# Revit family: P300298-009
name_source: partatom
category: Lighting Fixtures
revit_build: Autodesk Revit 2017 (Build: 20160225_1515(x64)
units: mm (PartAtom-declared; Revit-internal decimal feet)

## family parameters
Cut with Voids When Loaded = No
Host = Face
Light Source = No
OmniClass Number = 23.80.70.11.14.17
OmniClass Title = Direct/Indirect
Part Type = Normal
Room Calculation Point = No
Round Connector Dimension = Use Diameter
Shared = Yes

## types (1)
- P300298-009
    Apparent Load = 100 VA
    Assembly Code = D5020200
    Connector Description = Lighting Connector
    Default Elevation = 48 "
    Description = Conway Collection Four-Light Brushed Nickel and Clear Seeded Farmhouse Style Bath Vanity Wall Light
    Features = Mix old and new for charming character with the Conway Collection 4-Light Brushed Nickel Clear Seeded Farmhouse Bath Vanity Light. A brushed nickel bell-shaped frame and round backplate are accented by hand-painted, weathered grey wood-style accents for a charming nautical aesthetic. A light source glows from within a clear seeded glass shade for visual texture.
Application: Create a relaxing seaside haven with the Conway Collection 4-Light Brushed Nickel Clear Seeded Farmhouse Bath Vanity Light ideal for any entryway, hallway, foyer, bedroom, sitting room, living room, or bathroom.
Style: Perfect for farmhouse and coastal style settings.
Finish: A brushed nickel bell-shaped frame and round backplate are accented by hand-painted weathered grey wood-style accents for a charming nautical aesthetic.
Materials: Constructed from steel to ensure a long product lifespan. Mount the fixture facing up or down.
Glass: A light source glows from within a clear seeded glass shade for visual texture.
Bulbs: For ideal illumination, use 4 medium base bulbs that are sold separately (100w max - LED/CFL/incandescent). Compatible with dimmable bulbs.
Dimensions: Measures 33-inch width by 8-1/4-inch height by 7-inch depth.
Certifications: cULus damp location listed.
Pairs With: Pairs with Hemsworth, Austelle, and Kempsey collections.
Warranty: Our 1-Year Limited Warranty guarantees your complete satisfaction with your purchase and includes professional after-sales customer service support.
    Fixture distribution = Direct
    Glass = Paint - Hubbell - White Texture
    Housing Material = Paint - Hubbell - Metallic Silver Textured
    Lamp = LED/CFL/incandescent
    Load Classification = Lighting
    Manufacturer = Progress Lighting
    Model = P300298-009
    Power Factor = 1
    Product Documentation Link = https://hubbellcdn.com
    Product Link = https://www.hubbell.com
    URL = https://www.hubbell.com
    Voltage = 120 V
    Warranty = 1 year Warranty
    Wattage Comments = 100W
    Watts = 100 W
    Wood = Paint- Wood

## geometry (parser evidence)
native form markers: Sweep x6
no freeform markers — native parametric forms only
